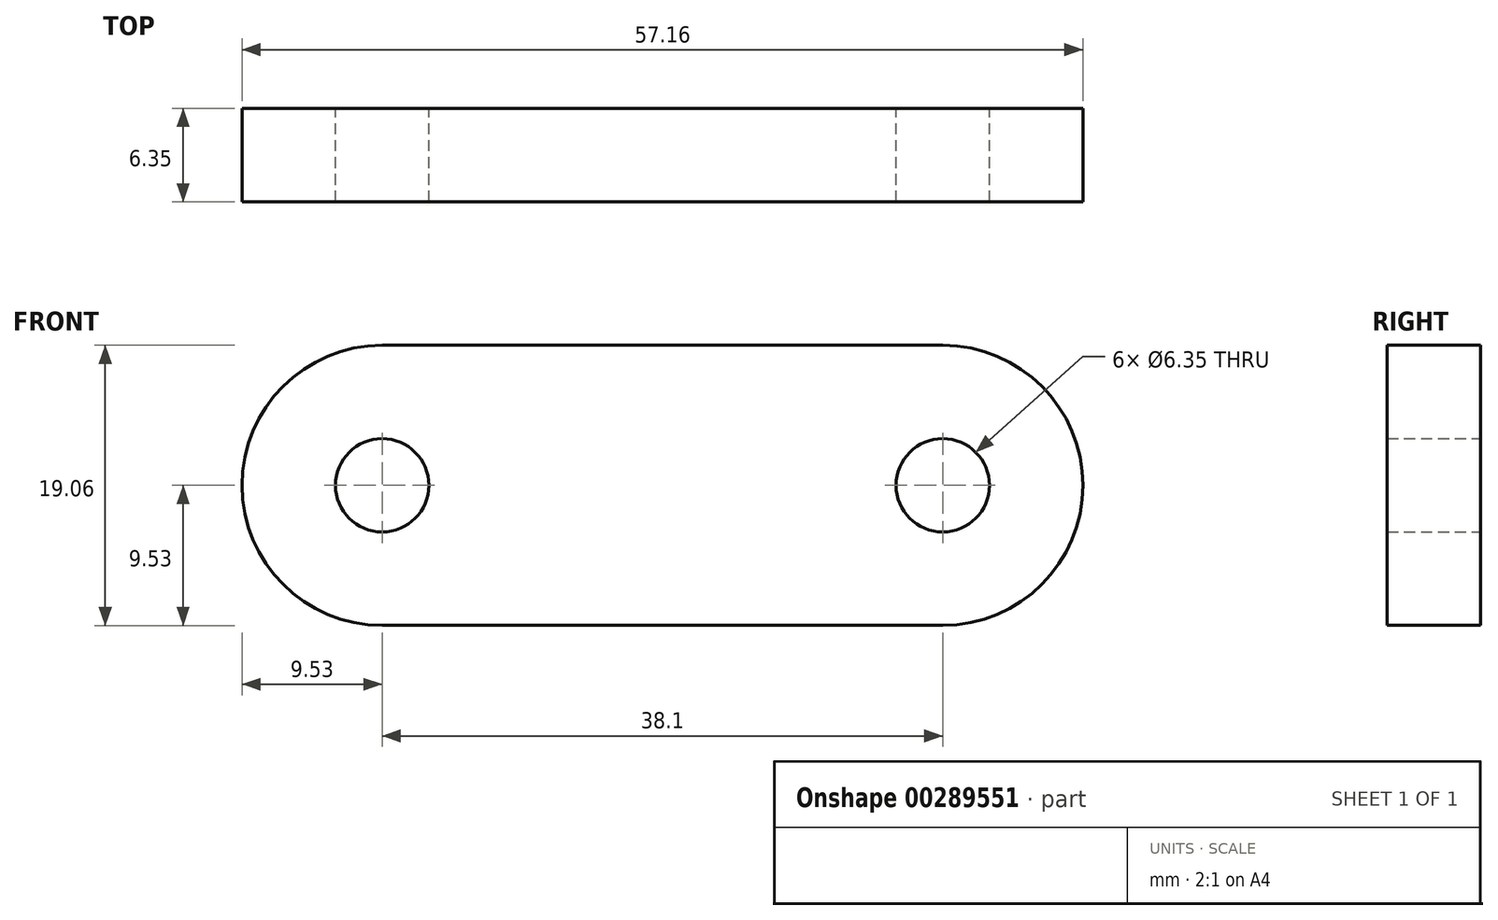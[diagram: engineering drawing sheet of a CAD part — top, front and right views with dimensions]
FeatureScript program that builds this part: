
annotation { "Feature Type Name" : "Feature", "Feature Type Description" : "" }
export const myFeature = defineFeature(function(context is Context, id is Id, definition is map)
    precondition{}
    {
        {
            var Q0;
            Q0=qCreatedBy(makeId("Front.planeOp"),FACE);
            var sketch = newSketch(context, id + "F0", { "sketchPlane" : qUnion([Q0])});
            skLineSegment(sketch, "E0.bottom", {"start": v(19.05, 9.53) * mm, "end": v(-19.05, 9.53) * mm});
            skLineSegment(sketch, "E0.top", {"start": v(19.05, -9.52) * mm, "end": v(-19.05, -9.52) * mm});
            skLineSegment(sketch, "E0.left", {"start": v(19.05, 9.53) * mm, "end": v(19.05, -9.53) * mm});
            skLineSegment(sketch, "E0.right", {"start": v(-19.05, 9.53) * mm, "end": v(-19.05, -9.52) * mm});
            skPoint(sketch, "E0.middle", {"position": v(0, 0) * mm});
            skCircle(sketch, "E1", {"center": v(19.05, 0) * mm, "radius": 3.18 * mm});
            skLineSegment(sketch, "E2", {"start": v(0, 9.52) * mm, "end": v(0, -9.52) * mm, "construction": true});
            skCircle(sketch, "E3.MirrorC", {"center": v(-19.05, 0) * mm, "radius": 3.18 * mm});
            skArc(sketch, "E4", {"start": v(19.05, -9.52) * mm, "mid": v(28.58, 0) * mm, "end": v(19.05, 9.53) * mm});
            skArc(sketch, "E5", {"start": v(-19.05, 9.53) * mm, "mid": v(-28.58, 0) * mm, "end": v(-19.05, -9.53) * mm});
            skSolve(sketch);
        }
        {
            var Q0;
            {var subQ5=sQuery(id+"F0.wireOp",EDGE,"E0.bottom");Q0=makeQuery(id+"F0.imprint","IMPRINT",FACE,{"disambiguationData":[TD([[makeQuery(id+"F0.imprint","IMPRINT",EDGE,{"derivedFrom":subQ5}),1.0]])]});}
            var Q1;
            {var subQ0=sQuery(id+"F0.wireOp",EDGE,"E5");Q1=makeQuery(id+"F0.imprint","IMPRINT",FACE,{"disambiguationData":[TD([[makeQuery(id+"F0.imprint","IMPRINT",EDGE,{"derivedFrom":subQ0}),1.0]])]});}
            var Q2;
            {var subQ0=sQuery(id+"F0.wireOp",EDGE,"E4");Q2=makeQuery(id+"F0.imprint","IMPRINT",FACE,{"disambiguationData":[TD([[makeQuery(id+"F0.imprint","IMPRINT",EDGE,{"derivedFrom":subQ0}),1.0]])]});}
            extrude(context, id + "F1", {"entities" : qUnion([Q0, Q1, Q2]), "depth" : 6.35 * mm});
        }
    });
